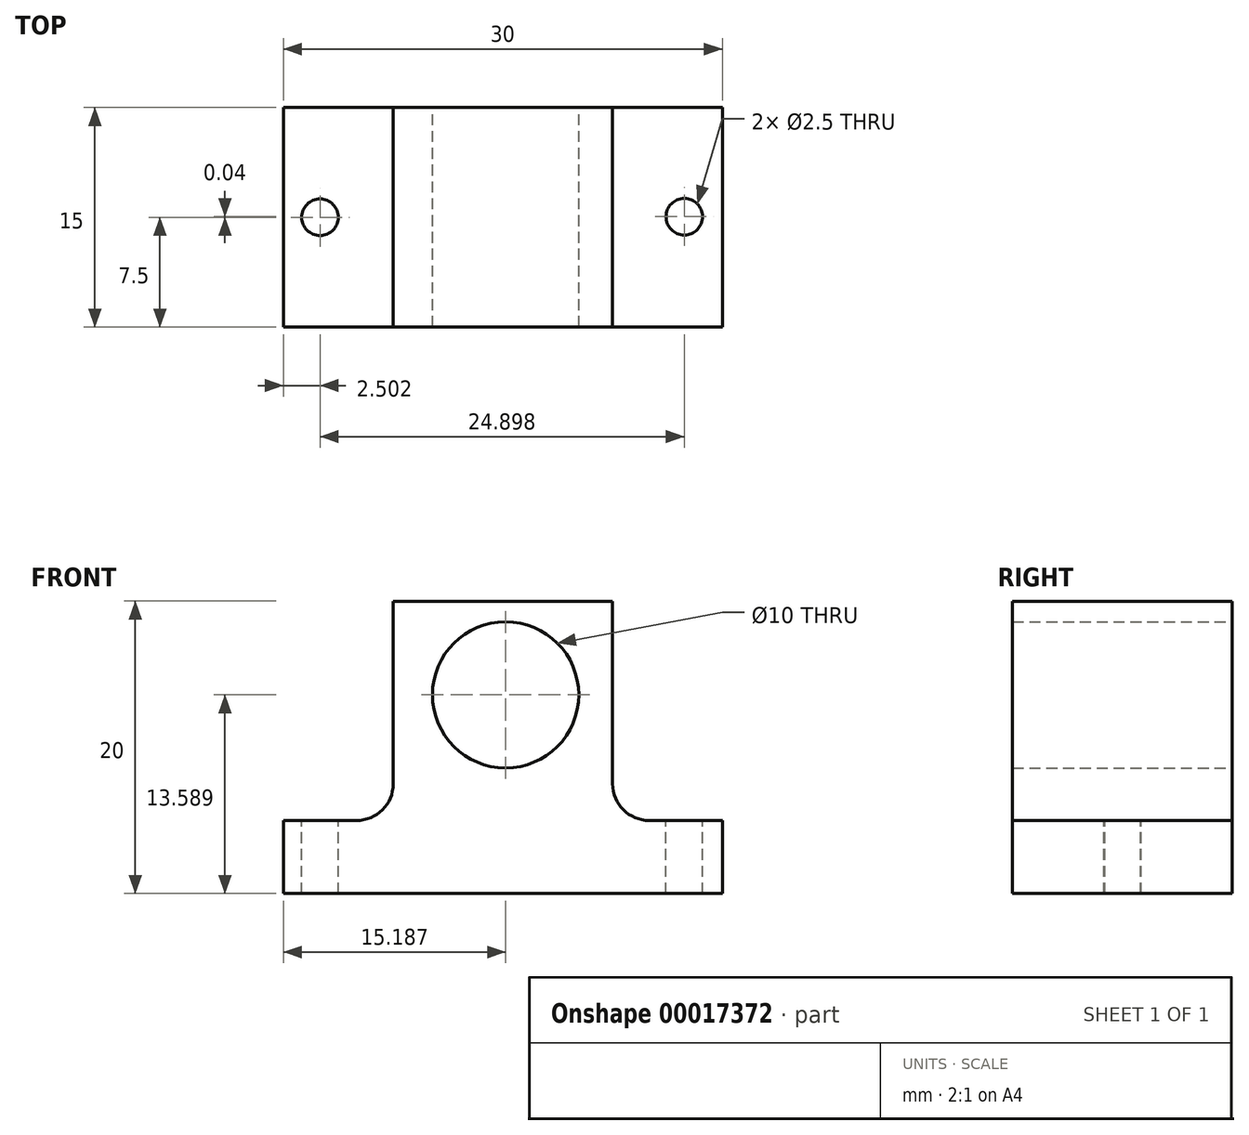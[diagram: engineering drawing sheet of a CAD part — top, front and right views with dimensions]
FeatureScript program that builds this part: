
annotation { "Feature Type Name" : "Feature", "Feature Type Description" : "" }
export const myFeature = defineFeature(function(context is Context, id is Id, definition is map)
    precondition{}
    {
        {
            var Q0;
            Q0=qCreatedBy(makeId("Front.planeOp"),FACE);
            var sketch = newSketch(context, id + "F0", { "sketchPlane" : qUnion([Q0])});
            skLineSegment(sketch, "E0", {"start": v(-11.15, 18.16) * mm, "end": v(-11.15, 5.66) * mm});
            skLineSegment(sketch, "E1", {"start": v(-13.65, 3.16) * mm, "end": v(-18.65, 3.16) * mm});
            skLineSegment(sketch, "E2", {"start": v(-18.65, 3.16) * mm, "end": v(-18.65, -1.84) * mm});
            skLineSegment(sketch, "E3", {"start": v(-18.65, -1.84) * mm, "end": v(11.35, -1.84) * mm});
            skLineSegment(sketch, "E4", {"start": v(11.35, -1.84) * mm, "end": v(11.35, 3.16) * mm});
            skLineSegment(sketch, "E5", {"start": v(11.35, 3.16) * mm, "end": v(6.35, 3.16) * mm});
            skLineSegment(sketch, "E6", {"start": v(3.85, 5.66) * mm, "end": v(3.85, 18.16) * mm});
            skLineSegment(sketch, "E7", {"start": v(3.85, 18.16) * mm, "end": v(-11.15, 18.16) * mm});
            skPoint(sketch, "E8.visualSharp", {"position": v(3.85, 3.16) * mm});
            skArc(sketch, "E8.filletArc", {"start": v(3.85, 5.66) * mm, "mid": v(4.58, 3.89) * mm, "end": v(6.35, 3.16) * mm});
            skPoint(sketch, "E9.visualSharp", {"position": v(-11.15, 3.16) * mm});
            skArc(sketch, "E9.filletArc", {"start": v(-13.65, 3.16) * mm, "mid": v(-11.88, 3.89) * mm, "end": v(-11.15, 5.66) * mm});
            skCircle(sketch, "E10", {"center": v(-3.46, 11.75) * mm, "radius": 5 * mm});
            skSolve(sketch);
        }
        {
            var Q0;
            Q0=makeQuery(id+"F0.imprint","IMPRINT",FACE,{"disambiguationData":[TD([[makeQuery(id+"F0.imprint","IMPRINT",EDGE,{"derivedFrom":sQuery(id+"F0.wireOp",EDGE,"E0")}),1.0]])]});
            extrude(context, id + "F1", {"entities" : qUnion([Q0]), "depth" : 15 * mm});
        }
        {
            var Q0;
            Q0=makeQuery(id+"F1.opExtrude","SWEPT_FACE",FACE,{"disambiguationData":[OSD([sQuery(id+"F0.wireOp",EDGE,"E1")])]});
            var sketch = newSketch(context, id + "F2", { "sketchPlane" : qUnion([Q0])});
            skCircle(sketch, "E11", {"center": v(-16.15, -7.5) * mm, "radius": 1.25 * mm});
            skSolve(sketch);
        }
        {
            var Q0;
            Q0=makeQuery(id+"F2.imprint","IMPRINT",FACE,{"disambiguationData":[TD([[makeQuery(id+"F2.imprint","IMPRINT",EDGE,{"derivedFrom":sQuery(id+"F2.wireOp",EDGE,"E11")}),1.0]])]});
            extrude(context, id + "F3", {"entities" : qUnion([Q0]), "operationType" : NewBodyOperationType.REMOVE, "oppositeDirection" : true, "depth" : 25 * mm});
        }
        {
            var Q0;
            Q0=makeQuery(id+"F1.opExtrude","SWEPT_FACE",FACE,{"disambiguationData":[OSD([sQuery(id+"F0.wireOp",EDGE,"E5")])]});
            var sketch = newSketch(context, id + "F4", { "sketchPlane" : qUnion([Q0])});
            skCircle(sketch, "E12", {"center": v(8.75, -7.46) * mm, "radius": 1.25 * mm});
            skSolve(sketch);
        }
        {
            var Q0;
            Q0=makeQuery(id+"F4.imprint","IMPRINT",FACE,{"disambiguationData":[TD([[makeQuery(id+"F4.imprint","IMPRINT",EDGE,{"derivedFrom":sQuery(id+"F4.wireOp",EDGE,"E12")}),1.0]])]});
            extrude(context, id + "F5", {"entities" : qUnion([Q0]), "operationType" : NewBodyOperationType.REMOVE, "oppositeDirection" : true, "depth" : 25 * mm});
        }
    });
